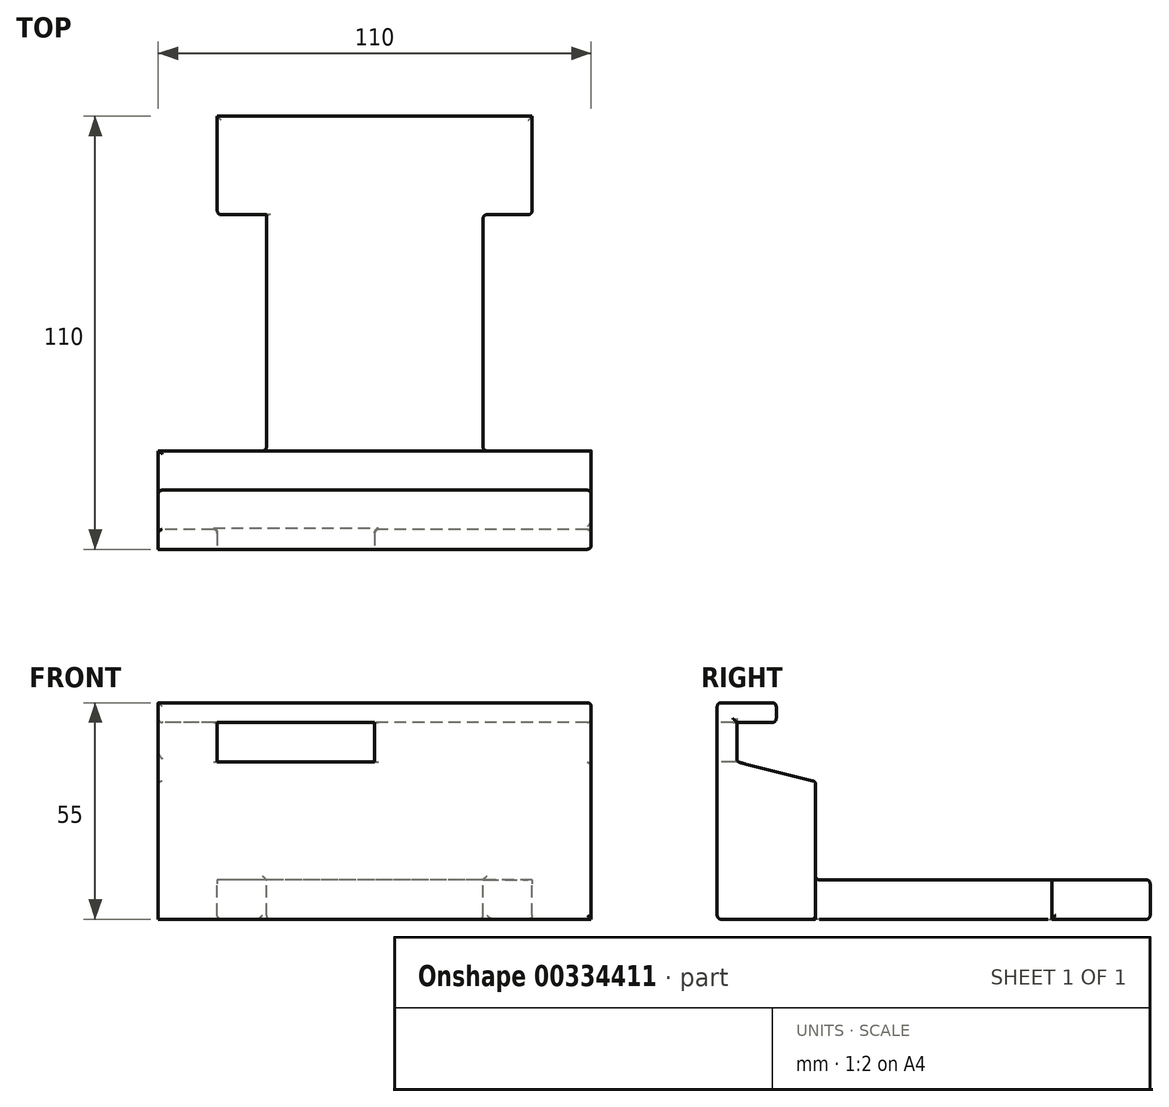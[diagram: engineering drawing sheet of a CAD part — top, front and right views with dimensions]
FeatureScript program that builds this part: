
annotation { "Feature Type Name" : "Feature", "Feature Type Description" : "" }
export const myFeature = defineFeature(function(context is Context, id is Id, definition is map)
    precondition{}
    {
        {
            var Q0;
            Q0=qCreatedBy(makeId("Right.planeOp"),FACE);
            var sketch = newSketch(context, id + "F0", { "sketchPlane" : qUnion([Q0])});
            skLineSegment(sketch, "E0", {"start": v(0, 0) * mm, "end": v(-110, 0) * mm});
            skLineSegment(sketch, "E1", {"start": v(0, 0) * mm, "end": v(0, 10) * mm});
            skLineSegment(sketch, "E2", {"start": v(-110, 0) * mm, "end": v(-110, 55) * mm});
            skLineSegment(sketch, "E3", {"start": v(-110, 55) * mm, "end": v(-95, 55) * mm});
            skLineSegment(sketch, "E4", {"start": v(-95, 55) * mm, "end": v(-95, 50) * mm});
            skLineSegment(sketch, "E5", {"start": v(-95, 50) * mm, "end": v(-105, 50) * mm});
            skLineSegment(sketch, "E6", {"start": v(-105, 50) * mm, "end": v(-105, 40) * mm});
            skLineSegment(sketch, "E7", {"start": v(0, 10) * mm, "end": v(-85, 10) * mm});
            skLineSegment(sketch, "E8", {"start": v(-85, 10) * mm, "end": v(-85, 35) * mm});
            skLineSegment(sketch, "E9", {"start": v(-105, 40) * mm, "end": v(-85, 35) * mm});
            skSolve(sketch);
        }
        {
            var Q0;
            Q0 = qSketchRegion(id + "F0", true);
            extrude(context, id + "F1", {"entities" : qUnion([Q0]), "endBound" : BoundingType.SYMMETRIC, "depth" : 110 * mm});
        }
        {
            var Q0;
            Q0=makeQuery(id+"F1.opExtrude","SWEPT_FACE",FACE,{"disambiguationData":[OSD([sQuery(id+"F0.wireOp",EDGE,"E7")])]});
            var sketch = newSketch(context, id + "F2", { "sketchPlane" : qUnion([Q0])});
            skPoint(sketch, "E10.start.orphan", {"position": v(0, 0) * mm});
            skLineSegment(sketch, "E11.bottom", {"start": v(55, -85) * mm, "end": v(27.5, -85) * mm});
            skLineSegment(sketch, "E11.left", {"start": v(55, -85) * mm, "end": v(55, -25) * mm});
            skLineSegment(sketch, "E11.right", {"start": v(27.5, -85) * mm, "end": v(27.5, -25) * mm});
            skLineSegment(sketch, "E12.bottom", {"start": v(-55, -85) * mm, "end": v(-27.5, -85) * mm});
            skLineSegment(sketch, "E12.left", {"start": v(-55, -85) * mm, "end": v(-55, -25) * mm});
            skLineSegment(sketch, "E12.right", {"start": v(-27.5, -85) * mm, "end": v(-27.5, -25) * mm});
            skLineSegment(sketch, "E13", {"start": v(0, 0) * mm, "end": v(40, 0) * mm});
            skLineSegment(sketch, "E14", {"start": v(0, 0) * mm, "end": v(-40, 0) * mm});
            skLineSegment(sketch, "E15", {"start": v(40, 0) * mm, "end": v(40, -25) * mm});
            skLineSegment(sketch, "E16", {"start": v(27.5, -25) * mm, "end": v(40, -25) * mm});
            skLineSegment(sketch, "E17", {"start": v(-40, 0) * mm, "end": v(-40, -25) * mm});
            skLineSegment(sketch, "E18", {"start": v(-27.5, -25) * mm, "end": v(-40, -25) * mm});
            skLineSegment(sketch, "E19", {"start": v(-40, 0) * mm, "end": v(-55, 0) * mm});
            skLineSegment(sketch, "E20", {"start": v(-55, 0) * mm, "end": v(-55, -25) * mm});
            skLineSegment(sketch, "E21", {"start": v(40, 0) * mm, "end": v(55, 0) * mm});
            skLineSegment(sketch, "E22", {"start": v(55, 0) * mm, "end": v(55, -25) * mm});
            skSolve(sketch);
        }
        {
            var Q0;
            Q0 = qSketchRegion(id + "F2", true);
            extrude(context, id + "F3", {"entities" : qUnion([Q0]), "operationType" : NewBodyOperationType.REMOVE, "endBound" : BoundingType.THROUGH_ALL, "oppositeDirection" : true, "depth" : 25 * mm});
        }
        {
            var Q0;
            Q0=makeQuery(id+"F1.opExtrude","SWEPT_FACE",FACE,{"disambiguationData":[OSD([sQuery(id+"F0.wireOp",EDGE,"E2")])]});
            var sketch = newSketch(context, id + "F4", { "sketchPlane" : qUnion([Q0])});
            skLineSegment(sketch, "E23.bottom", {"start": v(-40, 50) * mm, "end": v(0, 50) * mm});
            skLineSegment(sketch, "E23.top", {"start": v(-40, 40) * mm, "end": v(0, 40) * mm});
            skLineSegment(sketch, "E23.left", {"start": v(-40, 50) * mm, "end": v(-40, 40) * mm});
            skLineSegment(sketch, "E23.right", {"start": v(0, 50) * mm, "end": v(0, 40) * mm});
            skSolve(sketch);
        }
        {
            var Q0;
            Q0=makeQuery(id+"F1.opExtrude","SWEPT_EDGE",EDGE,{"disambiguationData":[OSD([sQuery(id+"F0.wireOp",EDGE,"E7"),sQuery(id+"F0.wireOp",EDGE,"E8")])]});
            var Q1;
            Q1=makeQuery(id+"F3.boolean.opBoolean","COPY",EDGE,{"derivedFrom":makeQuery(id+"F3.opExtrude","SWEPT_EDGE",EDGE,{"disambiguationData":[OSD([sQuery(id+"F0.wireOp",EDGE,"E7"),sQuery(id+"F0.wireOp",EDGE,"E8"),sQuery(id+"F2.wireOp",EDGE,"E11.bottom"),sQuery(id+"F2.wireOp",EDGE,"E11.right")])]})});
            var Q2;
            Q2=makeQuery(id+"F3.boolean.opBoolean","COPY",EDGE,{"derivedFrom":makeQuery(id+"F3.opExtrude","SWEPT_EDGE",EDGE,{"disambiguationData":[OSD([sQuery(id+"F0.wireOp",EDGE,"E7"),sQuery(id+"F0.wireOp",EDGE,"E8"),sQuery(id+"F2.wireOp",EDGE,"E12.bottom"),sQuery(id+"F2.wireOp",EDGE,"E12.right")])]})});
            var Q3;
            Q3=makeQuery(id+"F3.boolean.opBoolean","MERGE",EDGE,{"derivedFrom":[makeQuery(id+"F1.opExtrude","CAP_EDGE",EDGE,{"disambiguationData":[OSD([sQuery(id+"F0.wireOp",EDGE,"E8")])],"isStart":true}),makeQuery(id+"F3.opExtrude","SWEPT_EDGE",EDGE,{"disambiguationData":[OSD([sQuery(id+"F2.wireOp",EDGE,"E12.bottom"),sQuery(id+"F2.wireOp",EDGE,"E12.left")])]})]});
            var Q4;
            Q4=makeQuery(id+"F1.opExtrude","SWEPT_EDGE",EDGE,{"disambiguationData":[OSD([sQuery(id+"F0.wireOp",EDGE,"E8"),sQuery(id+"F0.wireOp",EDGE,"E9")])]});
            var Q5;
            Q5=makeQuery(id+"F1.opExtrude","CAP_EDGE",EDGE,{"disambiguationData":[OSD([sQuery(id+"F0.wireOp",EDGE,"E9")])],"isStart":true});
            var Q6;
            Q6=makeQuery(id+"F1.opExtrude","SWEPT_EDGE",EDGE,{"disambiguationData":[OSD([sQuery(id+"F0.wireOp",EDGE,"E6"),sQuery(id+"F0.wireOp",EDGE,"E9")])]});
            var Q7;
            Q7=makeQuery(id+"F3.boolean.opBoolean","MERGE",EDGE,{"derivedFrom":[makeQuery(id+"F1.opExtrude","CAP_EDGE",EDGE,{"disambiguationData":[OSD([sQuery(id+"F0.wireOp",EDGE,"E8")])],"isStart":false}),makeQuery(id+"F3.opExtrude","SWEPT_EDGE",EDGE,{"disambiguationData":[OSD([sQuery(id+"F2.wireOp",EDGE,"E11.bottom"),sQuery(id+"F2.wireOp",EDGE,"E11.left")])]})]});
            var Q8;
            Q8=makeQuery(id+"F3.boolean.opBoolean","COPY",EDGE,{"derivedFrom":makeQuery(id+"F3.opExtrude","CAP_EDGE",EDGE,{"disambiguationData":[OSD([sQuery(id+"F2.wireOp",EDGE,"E12.right")])],"isStart":true})});
            var Q9;
            Q9=makeQuery(id+"F3.boolean.opBoolean","INTERSECT",EDGE,{"derivedFrom":[makeQuery(id+"F1.opExtrude","SWEPT_FACE",FACE,{"disambiguationData":[OSD([sQuery(id+"F0.wireOp",EDGE,"E0")])]}),makeQuery(id+"F3.opExtrude","SWEPT_FACE",FACE,{"disambiguationData":[OSD([sQuery(id+"F2.wireOp",EDGE,"E12.right")])]})]});
            var Q10;
            Q10=makeQuery(id+"F3.boolean.opBoolean","COPY",EDGE,{"derivedFrom":makeQuery(id+"F3.opExtrude","CAP_EDGE",EDGE,{"disambiguationData":[OSD([sQuery(id+"F2.wireOp",EDGE,"E18")])],"isStart":true})});
            var Q11;
            Q11=makeQuery(id+"F3.boolean.opBoolean","COPY",EDGE,{"derivedFrom":makeQuery(id+"F3.opExtrude","SWEPT_EDGE",EDGE,{"disambiguationData":[OSD([sQuery(id+"F2.wireOp",EDGE,"E17"),sQuery(id+"F2.wireOp",EDGE,"E18")])]})});
            var Q12;
            Q12=makeQuery(id+"F3.boolean.opBoolean","INTERSECT",EDGE,{"derivedFrom":[makeQuery(id+"F1.opExtrude","SWEPT_FACE",FACE,{"disambiguationData":[OSD([sQuery(id+"F0.wireOp",EDGE,"E0")])]}),makeQuery(id+"F3.opExtrude","SWEPT_FACE",FACE,{"disambiguationData":[OSD([sQuery(id+"F2.wireOp",EDGE,"E17")])]})]});
            var Q13;
            Q13=makeQuery(id+"F3.boolean.opBoolean","COPY",EDGE,{"derivedFrom":makeQuery(id+"F3.opExtrude","CAP_EDGE",EDGE,{"disambiguationData":[OSD([sQuery(id+"F2.wireOp",EDGE,"E17")])],"isStart":true})});
            var Q14;
            Q14=makeQuery(id+"F3.boolean.opBoolean","COPY",EDGE,{"derivedFrom":makeQuery(id+"F3.opExtrude","SWEPT_EDGE",EDGE,{"disambiguationData":[OSD([sQuery(id+"F2.wireOp",EDGE,"E14"),sQuery(id+"F2.wireOp",EDGE,"E17"),sQuery(id+"F2.wireOp",EDGE,"E19")])]})});
            var Q15;
            Q15=makeQuery(id+"F1.opExtrude","SWEPT_EDGE",EDGE,{"disambiguationData":[OSD([sQuery(id+"F0.wireOp",EDGE,"E1"),sQuery(id+"F0.wireOp",EDGE,"E7")])]});
            var Q16;
            Q16=makeQuery(id+"F1.opExtrude","SWEPT_EDGE",EDGE,{"disambiguationData":[OSD([sQuery(id+"F0.wireOp",EDGE,"E0"),sQuery(id+"F0.wireOp",EDGE,"E1")])]});
            var Q17;
            Q17=makeQuery(id+"F3.boolean.opBoolean","COPY",EDGE,{"derivedFrom":makeQuery(id+"F3.opExtrude","CAP_EDGE",EDGE,{"disambiguationData":[OSD([sQuery(id+"F2.wireOp",EDGE,"E11.right")])],"isStart":true})});
            var Q18;
            Q18=makeQuery(id+"F3.boolean.opBoolean","COPY",EDGE,{"derivedFrom":makeQuery(id+"F3.opExtrude","CAP_EDGE",EDGE,{"disambiguationData":[OSD([sQuery(id+"F2.wireOp",EDGE,"E16")])],"isStart":true})});
            var Q19;
            Q19=makeQuery(id+"F3.boolean.opBoolean","COPY",EDGE,{"derivedFrom":makeQuery(id+"F3.opExtrude","CAP_EDGE",EDGE,{"disambiguationData":[OSD([sQuery(id+"F2.wireOp",EDGE,"E15")])],"isStart":true})});
            var Q20;
            Q20=makeQuery(id+"F3.boolean.opBoolean","COPY",EDGE,{"derivedFrom":makeQuery(id+"F3.opExtrude","SWEPT_EDGE",EDGE,{"disambiguationData":[OSD([sQuery(id+"F2.wireOp",EDGE,"E13"),sQuery(id+"F2.wireOp",EDGE,"E15"),sQuery(id+"F2.wireOp",EDGE,"E21")])]})});
            var Q21;
            Q21=makeQuery(id+"F3.boolean.opBoolean","COPY",EDGE,{"derivedFrom":makeQuery(id+"F3.opExtrude","SWEPT_EDGE",EDGE,{"disambiguationData":[OSD([sQuery(id+"F2.wireOp",EDGE,"E15"),sQuery(id+"F2.wireOp",EDGE,"E16")])]})});
            var Q22;
            Q22=makeQuery(id+"F3.boolean.opBoolean","COPY",EDGE,{"derivedFrom":makeQuery(id+"F3.opExtrude","SWEPT_EDGE",EDGE,{"disambiguationData":[OSD([sQuery(id+"F2.wireOp",EDGE,"E11.right"),sQuery(id+"F2.wireOp",EDGE,"E16")])]})});
            var Q23;
            Q23=makeQuery(id+"F3.boolean.opBoolean","INTERSECT",EDGE,{"derivedFrom":[makeQuery(id+"F1.opExtrude","SWEPT_FACE",FACE,{"disambiguationData":[OSD([sQuery(id+"F0.wireOp",EDGE,"E0")])]}),makeQuery(id+"F3.opExtrude","SWEPT_FACE",FACE,{"disambiguationData":[OSD([sQuery(id+"F2.wireOp",EDGE,"E11.right")])]})]});
            var Q24;
            Q24=makeQuery(id+"F3.boolean.opBoolean","INTERSECT",EDGE,{"derivedFrom":[makeQuery(id+"F1.opExtrude","SWEPT_FACE",FACE,{"disambiguationData":[OSD([sQuery(id+"F0.wireOp",EDGE,"E0")])]}),makeQuery(id+"F3.opExtrude","SWEPT_FACE",FACE,{"disambiguationData":[OSD([sQuery(id+"F2.wireOp",EDGE,"E15")])]})]});
            var Q25;
            Q25=makeQuery(id+"F1.opExtrude","CAP_EDGE",EDGE,{"disambiguationData":[OSD([sQuery(id+"F0.wireOp",EDGE,"E2")])],"isStart":false});
            var Q26;
            Q26=makeQuery(id+"F1.opExtrude","CAP_EDGE",EDGE,{"disambiguationData":[OSD([sQuery(id+"F0.wireOp",EDGE,"E3")])],"isStart":false});
            var Q27;
            Q27=makeQuery(id+"F1.opExtrude","CAP_EDGE",EDGE,{"disambiguationData":[OSD([sQuery(id+"F0.wireOp",EDGE,"E5")])],"isStart":false});
            var Q28;
            Q28=makeQuery(id+"F1.opExtrude","CAP_EDGE",EDGE,{"disambiguationData":[OSD([sQuery(id+"F0.wireOp",EDGE,"E6")])],"isStart":false});
            var Q29;
            Q29=makeQuery(id+"F1.opExtrude","SWEPT_EDGE",EDGE,{"disambiguationData":[OSD([sQuery(id+"F0.wireOp",EDGE,"E2"),sQuery(id+"F0.wireOp",EDGE,"E3")])]});
            var Q30;
            Q30=makeQuery(id+"F1.opExtrude","SWEPT_EDGE",EDGE,{"disambiguationData":[OSD([sQuery(id+"F0.wireOp",EDGE,"E0"),sQuery(id+"F0.wireOp",EDGE,"E2")])]});
            fillet(context, id + "F5", {"entities" : qUnion([Q0, Q1, Q2, Q3, Q4, Q5, Q6, Q7, Q8, Q9, Q10, Q11, Q12, Q13, Q14, Q15, Q16, Q17, Q18, Q19, Q20, Q21, Q22, Q23, Q24, Q25, Q26, Q27, Q28, Q29, Q30]), "radius" : 1 * mm, "tangentPropagation" : true, "allowEdgeOverflow" : false});
        }
        {
            var Q0;
            Q0 = qSketchRegion(id + "F4", true);
            extrude(context, id + "F6", {"entities" : qUnion([Q0]), "operationType" : NewBodyOperationType.REMOVE, "endBound" : BoundingType.THROUGH_ALL, "oppositeDirection" : true, "depth" : 25 * mm});
        }
        {
            var Q0;
            Q0=makeQuery(id+"F1.opExtrude","SWEPT_EDGE",EDGE,{"disambiguationData":[OSD([sQuery(id+"F0.wireOp",EDGE,"E4"),sQuery(id+"F0.wireOp",EDGE,"E5")])]});
            var Q1;
            Q1=makeQuery(id+"F1.opExtrude","CAP_EDGE",EDGE,{"disambiguationData":[OSD([sQuery(id+"F0.wireOp",EDGE,"E5")])],"isStart":true});
            var Q2;
            Q2=makeQuery(id+"F1.opExtrude","CAP_EDGE",EDGE,{"disambiguationData":[OSD([sQuery(id+"F0.wireOp",EDGE,"E4")])],"isStart":true});
            var Q3;
            Q3=makeQuery(id+"F6.boolean.opBoolean","INTERSECT",EDGE,{"derivedFrom":[makeQuery(id+"F1.opExtrude","SWEPT_FACE",FACE,{"disambiguationData":[OSD([sQuery(id+"F0.wireOp",EDGE,"E6")])]}),makeQuery(id+"F6.opExtrude","SWEPT_FACE",FACE,{"disambiguationData":[OSD([sQuery(id+"F4.wireOp",EDGE,"E23.right")])]})]});
            var Q4;
            Q4=makeQuery(id+"F6.boolean.opBoolean","COPY",EDGE,{"derivedFrom":makeQuery(id+"F6.opExtrude","CAP_EDGE",EDGE,{"disambiguationData":[OSD([sQuery(id+"F4.wireOp",EDGE,"E23.right")])],"isStart":true})});
            var Q5;
            Q5=makeQuery(id+"F6.boolean.opBoolean","INTERSECT",EDGE,{"derivedFrom":[makeQuery(id+"F1.opExtrude","SWEPT_FACE",FACE,{"disambiguationData":[OSD([sQuery(id+"F0.wireOp",EDGE,"E6")])]}),makeQuery(id+"F6.opExtrude","SWEPT_FACE",FACE,{"disambiguationData":[OSD([sQuery(id+"F4.wireOp",EDGE,"E23.left")])]})]});
            var Q6;
            Q6=makeQuery(id+"F6.boolean.opBoolean","COPY",EDGE,{"derivedFrom":makeQuery(id+"F6.opExtrude","CAP_EDGE",EDGE,{"disambiguationData":[OSD([sQuery(id+"F4.wireOp",EDGE,"E23.top")])],"isStart":true})});
            var Q7;
            Q7=makeQuery(id+"F6.boolean.opBoolean","COPY",EDGE,{"derivedFrom":makeQuery(id+"F6.opExtrude","CAP_EDGE",EDGE,{"disambiguationData":[OSD([sQuery(id+"F4.wireOp",EDGE,"E23.bottom")])],"isStart":true})});
            fillet(context, id + "F7", {"entities" : qUnion([Q0, Q1, Q2, Q3, Q4, Q5, Q6, Q7]), "radius" : 1 * mm, "tangentPropagation" : true, "allowEdgeOverflow" : false});
        }
    });
